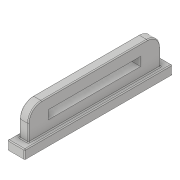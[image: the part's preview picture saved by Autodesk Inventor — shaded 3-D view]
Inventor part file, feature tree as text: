
AUTODESK INVENTOR PART (.ipt)
format: ipt  version: 2017 (Build 210142000, 142)  size: 138,752 bytes
history: native  units: in
note: dims shown in document units (in); Inventor stores cm internally (conversion verified against a paired STEP export)
features: extrude x2, sketch x2, fillet x1
ambient origin geometry x8: Origin, YZ Plane, XZ Plane, XY Plane, X Axis, Y Axis, Z Axis, Center Point
bodies: Solid1 (feature_tree)
feature tree (5):
  extrude  "Extrusion1"  Depth=6.0in
  extrude  "Extrusion2"  Depth=1.35in
  fillet  "Fillet1"  Radius=0.45in
  sketch  "Sketch1"  dims[d0=0.6in d1=6.0in]
  sketch  "Sketch3"  dims[d2=4.2in d3=1.35in d4=0.45in d5=0.4in d6=0.4in d7=0.0in d8=6.7in d9=0.78in d10=0.4in d11=0.0in d12=0.04in]
